# Revit family: Lighting-Recessed-Acclaim-TerraDrum
name_source: partatom
category: Lighting Fixtures
units: mm (PartAtom-declared; Revit-internal decimal feet)

## family parameters
Cut with Voids When Loaded = No
Host = Face
Light Source = Yes
Part Type = Normal
Room Calculation Point = No
Round Connector Dimension = Use Diameter
Shared = No

## types (3) — shared parameters
Apparent Load = 0 VA
Color Filter = 16777215
Default Elevation = 48 "
Description = Recessed
Dimming Lamp Color Temperature Shift = <None>
Emit from Line Length = 24 "
Height = 8.46 "
Housing Finish = Aluminum
Lamp = LED
Manufacturer = Acclaim Lighting
Model = Terra Drum
Number of Poles = 1
Photometric Web File = Load File
Power Factor = 1
Tilt Angle = -90.00°
URL = http://www.acclaimlighting.com
Voltage = 0 V

## per-type parameters (varying)
| type | Diameter |
| HO | 12.36 " |
| SO | 9.53 " |
| EO | 7.13 " |

## geometry (parser evidence)
native form markers: Blend x13, Sweep x3
no freeform markers — native parametric forms only
